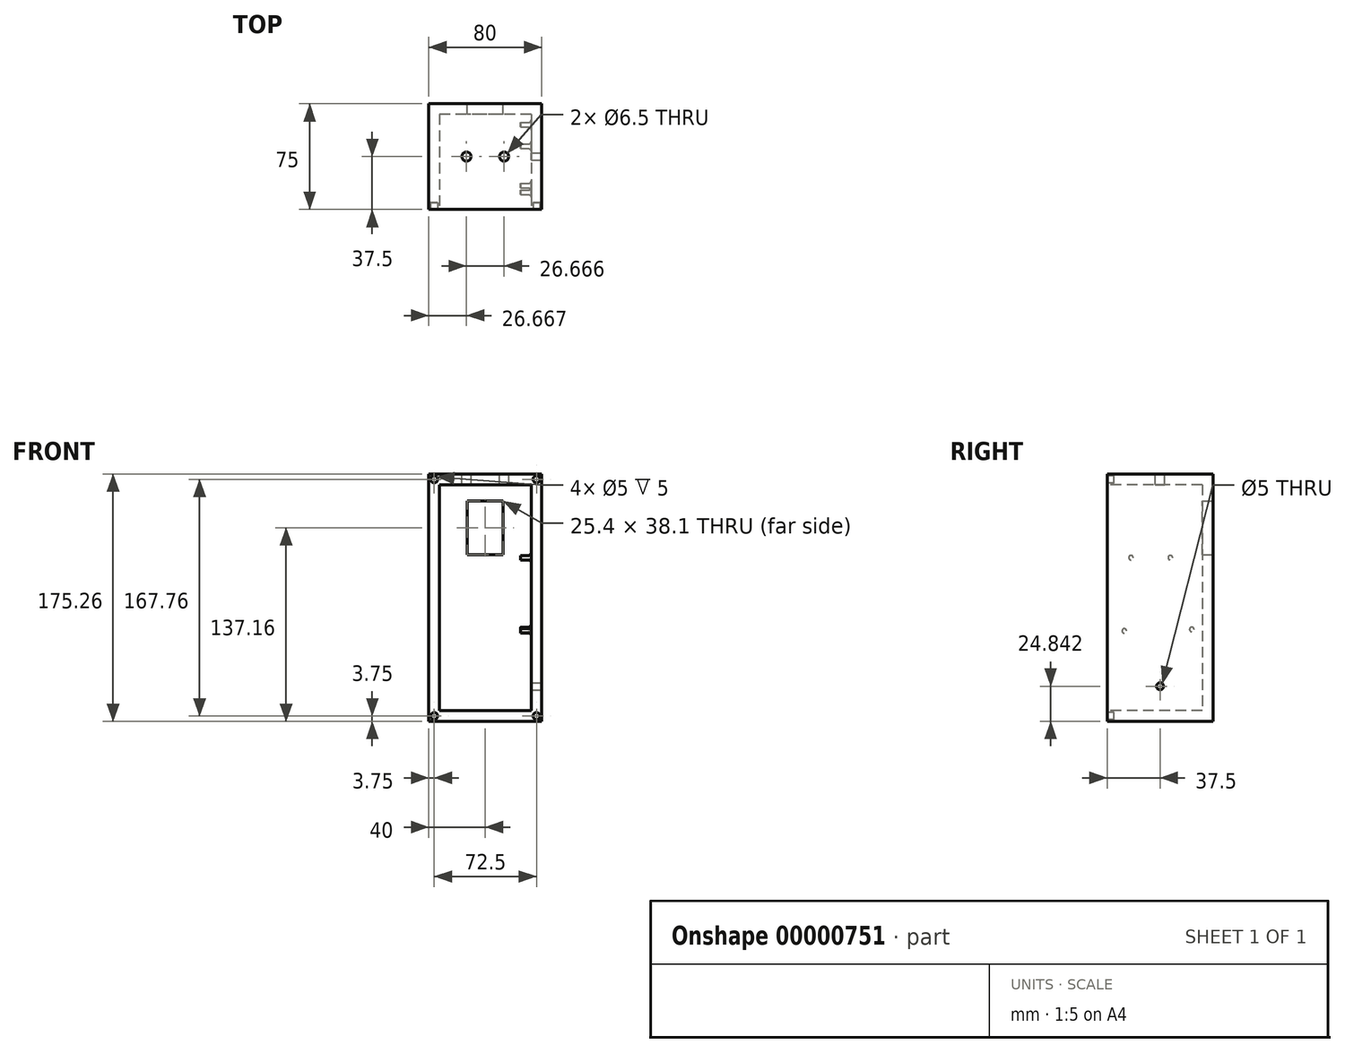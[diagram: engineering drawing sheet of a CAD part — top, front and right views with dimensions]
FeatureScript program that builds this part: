
annotation { "Feature Type Name" : "Feature", "Feature Type Description" : "" }
export const myFeature = defineFeature(function(context is Context, id is Id, definition is map)
    precondition{}
    {
        {
            var Q0;
            Q0=qCreatedBy(makeId("Front.planeOp"),FACE);
            var sketch = newSketch(context, id + "F0", { "sketchPlane" : qUnion([Q0])});
            skLineSegment(sketch, "E0", {"start": v(0, 0) * mm, "end": v(0, 175.26) * mm});
            skLineSegment(sketch, "E1", {"start": v(0, 175.26) * mm, "end": v(80, 175.26) * mm});
            skLineSegment(sketch, "E2", {"start": v(80, 175.26) * mm, "end": v(80, 0) * mm});
            skLineSegment(sketch, "E3", {"start": v(80, 0) * mm, "end": v(0, 0) * mm});
            skSolve(sketch);
        }
        {
            var Q0;
            Q0=makeQuery(id+"F0.imprint","IMPRINT",FACE,{"disambiguationData":[TD([[makeQuery(id+"F0.imprint","IMPRINT",EDGE,{"derivedFrom":sQuery(id+"F0.wireOp",EDGE,"E0")}),-1.0]])]});
            extrude(context, id + "F1", {"entities" : qUnion([Q0]), "depth" : 75 * mm});
        }
        {
            var Q0;
            Q0=makeQuery(id+"F1.opExtrude","CAP_FACE",FACE,{"disambiguationData":[OSD([sQuery(id+"F0.wireOp",EDGE,"E0"),sQuery(id+"F0.wireOp",EDGE,"E1"),sQuery(id+"F0.wireOp",EDGE,"E2"),sQuery(id+"F0.wireOp",EDGE,"E3")])],"isStart":false});
            var sketch = newSketch(context, id + "F2", { "sketchPlane" : qUnion([Q0])});
            skLineSegment(sketch, "E4", {"start": v(7.5, 167.76) * mm, "end": v(7.5, 7.5) * mm});
            skLineSegment(sketch, "E5", {"start": v(7.5, 7.5) * mm, "end": v(72.5, 7.5) * mm});
            skLineSegment(sketch, "E6", {"start": v(72.5, 7.5) * mm, "end": v(72.5, 167.76) * mm});
            skLineSegment(sketch, "E7", {"start": v(72.5, 167.76) * mm, "end": v(7.5, 167.76) * mm});
            skSolve(sketch);
        }
        {
            var Q0;
            Q0=makeQuery(id+"F2.imprint","IMPRINT",FACE,{"disambiguationData":[TD([[makeQuery(id+"F2.imprint","IMPRINT",EDGE,{"derivedFrom":sQuery(id+"F2.wireOp",EDGE,"E4")}),1.0]])]});
            extrude(context, id + "F3", {"entities" : qUnion([Q0]), "operationType" : NewBodyOperationType.REMOVE, "oppositeDirection" : true, "depth" : 67.5 * mm});
        }
        {
            var Q0;
            Q0=makeQuery(id+"F1.opExtrude","SWEPT_FACE",FACE,{"disambiguationData":[OSD([sQuery(id+"F0.wireOp",EDGE,"E1")])]});
            var sketch = newSketch(context, id + "F4", { "sketchPlane" : qUnion([Q0])});
            skCircle(sketch, "E8", {"center": v(53.33, -37.5) * mm, "radius": 3.25 * mm});
            skCircle(sketch, "E9", {"center": v(26.67, -37.5) * mm, "radius": 3.25 * mm});
            skSolve(sketch);
        }
        {
            var Q0;
            {Q0=qUnion([makeQuery(id+"F4.imprint","IMPRINT",FACE,{"disambiguationData":[TD([[makeQuery(id+"F4.imprint","IMPRINT",EDGE,{"derivedFrom":sQuery(id+"F4.wireOp",EDGE,"E8")}),1.0]])]}),makeQuery(id+"F4.imprint","IMPRINT",FACE,{"disambiguationData":[TD([[makeQuery(id+"F4.imprint","IMPRINT",EDGE,{"derivedFrom":sQuery(id+"F4.wireOp",EDGE,"E9")}),1.0]])]})]);}
            extrude(context, id + "F5", {"entities" : qUnion([Q0]), "operationType" : NewBodyOperationType.REMOVE, "oppositeDirection" : true, "depth" : 7.5 * mm});
        }
        {
            var Q0;
            Q0=makeQuery(id+"F1.opExtrude","CAP_FACE",FACE,{"disambiguationData":[OSD([sQuery(id+"F0.wireOp",EDGE,"E0"),sQuery(id+"F0.wireOp",EDGE,"E1"),sQuery(id+"F0.wireOp",EDGE,"E2"),sQuery(id+"F0.wireOp",EDGE,"E3")])],"isStart":false});
            var sketch = newSketch(context, id + "F6", { "sketchPlane" : qUnion([Q0])});
            skCircle(sketch, "E10", {"center": v(3.75, 171.51) * mm, "radius": 2.5 * mm});
            skCircle(sketch, "E11", {"center": v(76.25, 171.5) * mm, "radius": 2.5 * mm});
            skCircle(sketch, "E12", {"center": v(3.75, 3.75) * mm, "radius": 2.5 * mm});
            skCircle(sketch, "E13", {"center": v(76.25, 3.75) * mm, "radius": 2.5 * mm});
            skSolve(sketch);
        }
        {
            var Q0;
            {Q0=qUnion([makeQuery(id+"F6.imprint","IMPRINT",FACE,{"disambiguationData":[TD([[makeQuery(id+"F6.imprint","IMPRINT",EDGE,{"derivedFrom":sQuery(id+"F6.wireOp",EDGE,"E10")}),1.0]])]}),makeQuery(id+"F6.imprint","IMPRINT",FACE,{"disambiguationData":[TD([[makeQuery(id+"F6.imprint","IMPRINT",EDGE,{"derivedFrom":sQuery(id+"F6.wireOp",EDGE,"E11")}),1.0]])]}),makeQuery(id+"F6.imprint","IMPRINT",FACE,{"disambiguationData":[TD([[makeQuery(id+"F6.imprint","IMPRINT",EDGE,{"derivedFrom":sQuery(id+"F6.wireOp",EDGE,"E12")}),1.0]])]}),makeQuery(id+"F6.imprint","IMPRINT",FACE,{"disambiguationData":[TD([[makeQuery(id+"F6.imprint","IMPRINT",EDGE,{"derivedFrom":sQuery(id+"F6.wireOp",EDGE,"E13")}),1.0]])]})]);}
            extrude(context, id + "F7", {"entities" : qUnion([Q0]), "operationType" : NewBodyOperationType.REMOVE, "oppositeDirection" : true, "depth" : 5 * mm});
        }
        {
            var Q0;
            Q0=makeQuery(id+"F1.opExtrude","CAP_FACE",FACE,{"disambiguationData":[OSD([sQuery(id+"F0.wireOp",EDGE,"E0"),sQuery(id+"F0.wireOp",EDGE,"E1"),sQuery(id+"F0.wireOp",EDGE,"E2"),sQuery(id+"F0.wireOp",EDGE,"E3")])],"isStart":true});
            var sketch = newSketch(context, id + "F8", { "sketchPlane" : qUnion([Q0])});
            skLineSegment(sketch, "E14", {"start": v(-80, 175.26) * mm, "end": v(-40, 175.26) * mm, "construction": true});
            skLineSegment(sketch, "E15", {"start": v(-40, 175.26) * mm, "end": v(-40, 137.16) * mm, "construction": true});
            skLineSegment(sketch, "E16.rect.bottom", {"start": v(-27.3, 156.21) * mm, "end": v(-52.7, 156.21) * mm});
            skLineSegment(sketch, "E16.rect.top", {"start": v(-27.3, 118.11) * mm, "end": v(-52.7, 118.11) * mm});
            skLineSegment(sketch, "E16.rect.left", {"start": v(-27.3, 156.21) * mm, "end": v(-27.3, 118.11) * mm});
            skLineSegment(sketch, "E16.rect.right", {"start": v(-52.7, 156.21) * mm, "end": v(-52.7, 118.11) * mm});
            skPoint(sketch, "E16.rect.middle", {"position": v(-40, 137.16) * mm});
            skSolve(sketch);
        }
        {
            var Q0;
            Q0=makeQuery(id+"F8.imprint","IMPRINT",FACE,{"disambiguationData":[TD([[makeQuery(id+"F8.imprint","IMPRINT",EDGE,{"derivedFrom":sQuery(id+"F8.wireOp",EDGE,"E16.rect.bottom")}),1.0]])]});
            extrude(context, id + "F9", {"entities" : qUnion([Q0]), "operationType" : NewBodyOperationType.REMOVE, "oppositeDirection" : true, "depth" : 18.9 * mm});
        }
        {
            var Q0;
            Q0=makeQuery(id+"F1.opExtrude","SWEPT_FACE",FACE,{"disambiguationData":[OSD([sQuery(id+"F0.wireOp",EDGE,"E2")])]});
            var sketch = newSketch(context, id + "F10", { "sketchPlane" : qUnion([Q0])});
            skCircle(sketch, "E17", {"center": v(-58.1, 115.96) * mm, "radius": 1.6 * mm});
            skCircle(sketch, "E18", {"center": v(-30.2, 115.96) * mm, "radius": 1.6 * mm});
            skCircle(sketch, "E19", {"center": v(-62.8, 64.06) * mm, "radius": 1.6 * mm});
            skCircle(sketch, "E20", {"center": v(-15, 65.16) * mm, "radius": 1.6 * mm});
            skSolve(sketch);
        }
        {
            var Q0;
            Q0 = qSketchRegion(id + "F10", true);
            extrude(context, id + "F11", {"entities" : qUnion([Q0]), "operationType" : NewBodyOperationType.ADD, "oppositeDirection" : true, "depth" : 15 * mm});
        }
        {
            var Q0;
            Q0=makeQuery(id+"F11.boolean.opBoolean","INTERSECT",EDGE,{"derivedFrom":[makeQuery(id+"F3.boolean.opBoolean","COPY",FACE,{"derivedFrom":makeQuery(id+"F3.opExtrude","SWEPT_FACE",FACE,{"disambiguationData":[OSD([sQuery(id+"F2.wireOp",EDGE,"E6")])]})}),makeQuery(id+"F11.opExtrude","SWEPT_FACE",FACE,{"disambiguationData":[OSD([sQuery(id+"F10.wireOp",EDGE,"E17")])]})]});
            var Q1;
            Q1=makeQuery(id+"F11.boolean.opBoolean","INTERSECT",EDGE,{"derivedFrom":[makeQuery(id+"F3.boolean.opBoolean","COPY",FACE,{"derivedFrom":makeQuery(id+"F3.opExtrude","SWEPT_FACE",FACE,{"disambiguationData":[OSD([sQuery(id+"F2.wireOp",EDGE,"E6")])]})}),makeQuery(id+"F11.opExtrude","SWEPT_FACE",FACE,{"disambiguationData":[OSD([sQuery(id+"F10.wireOp",EDGE,"E18")])]})]});
            var Q2;
            Q2=makeQuery(id+"F11.boolean.opBoolean","INTERSECT",EDGE,{"derivedFrom":[makeQuery(id+"F3.boolean.opBoolean","COPY",FACE,{"derivedFrom":makeQuery(id+"F3.opExtrude","SWEPT_FACE",FACE,{"disambiguationData":[OSD([sQuery(id+"F2.wireOp",EDGE,"E6")])]})}),makeQuery(id+"F11.opExtrude","SWEPT_FACE",FACE,{"disambiguationData":[OSD([sQuery(id+"F10.wireOp",EDGE,"E20")])]})]});
            var Q3;
            Q3=makeQuery(id+"F11.boolean.opBoolean","INTERSECT",EDGE,{"derivedFrom":[makeQuery(id+"F3.boolean.opBoolean","COPY",FACE,{"derivedFrom":makeQuery(id+"F3.opExtrude","SWEPT_FACE",FACE,{"disambiguationData":[OSD([sQuery(id+"F2.wireOp",EDGE,"E6")])]})}),makeQuery(id+"F11.opExtrude","SWEPT_FACE",FACE,{"disambiguationData":[OSD([sQuery(id+"F10.wireOp",EDGE,"E19")])]})]});
            fillet(context, id + "F12", {"entities" : qUnion([Q0, Q1, Q2, Q3]), "radius" : 2 * mm, "tangentPropagation" : true, "allowEdgeOverflow" : false});
        }
        {
            var Q0;
            Q0=makeQuery(id+"F1.opExtrude","SWEPT_FACE",FACE,{"disambiguationData":[OSD([sQuery(id+"F0.wireOp",EDGE,"E2")])]});
            var sketch = newSketch(context, id + "F13", { "sketchPlane" : qUnion([Q0])});
            skCircle(sketch, "E21", {"center": v(-37.5, 24.84) * mm, "radius": 2.5 * mm});
            skSolve(sketch);
        }
        {
            var Q0;
            Q0 = qSketchRegion(id + "F13", true);
            extrude(context, id + "F14", {"entities" : qUnion([Q0]), "operationType" : NewBodyOperationType.REMOVE, "endBound" : BoundingType.UP_TO_NEXT, "oppositeDirection" : true, "depth" : 25.4 * mm});
        }
    });
